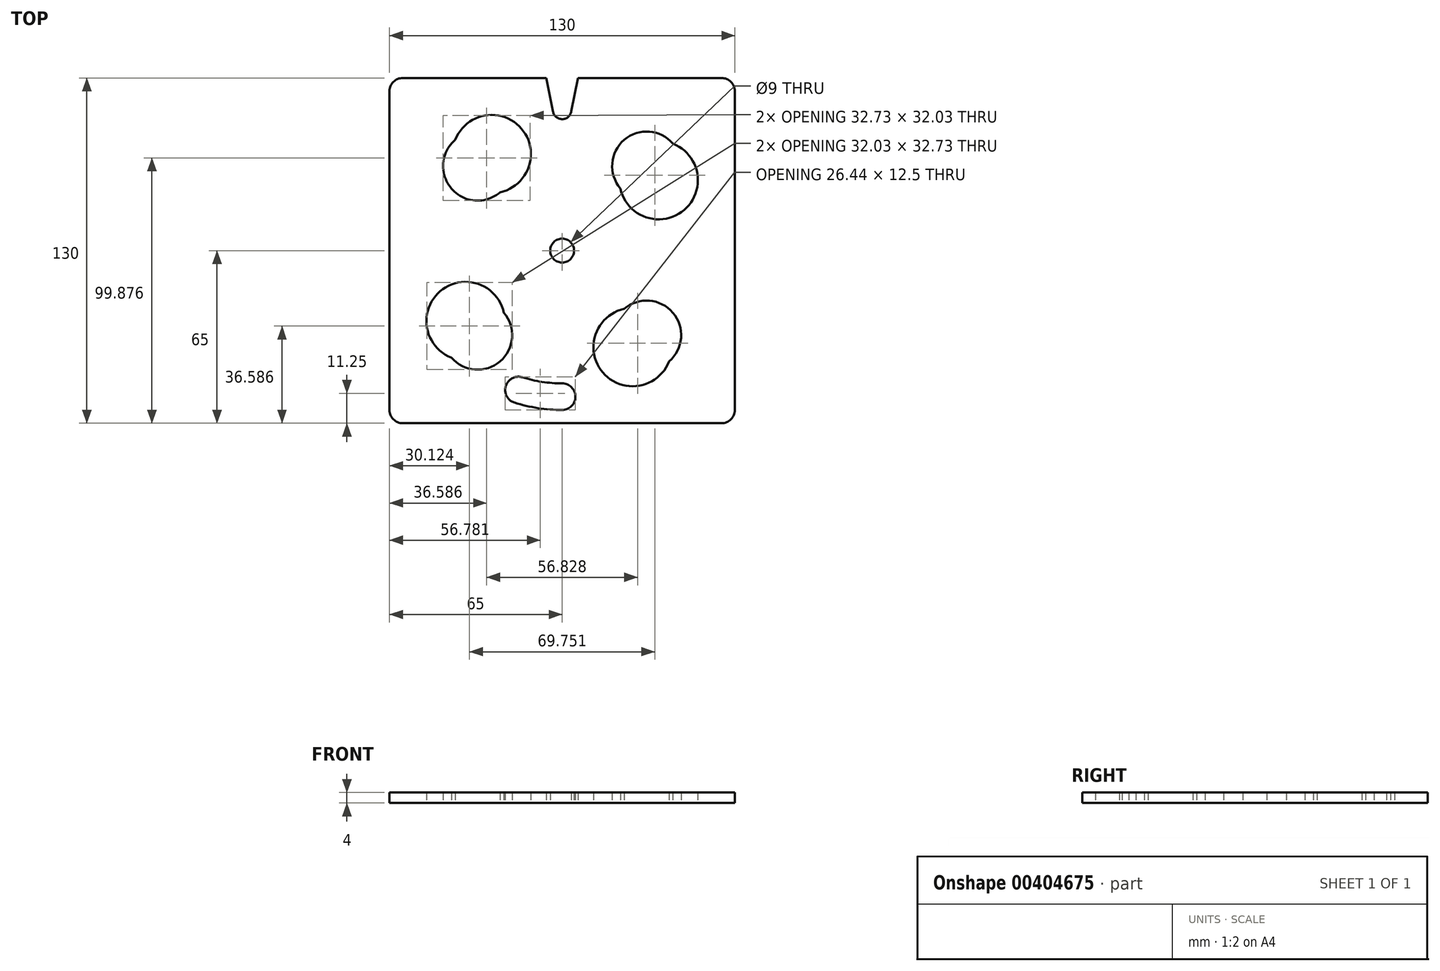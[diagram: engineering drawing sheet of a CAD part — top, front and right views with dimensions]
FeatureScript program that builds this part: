
annotation { "Feature Type Name" : "Feature", "Feature Type Description" : "" }
export const myFeature = defineFeature(function(context is Context, id is Id, definition is map)
    precondition{}
    {
        {
            var Q0;
            Q0=qCreatedBy(makeId("Top.planeOp"),FACE);
            var sketch = newSketch(context, id + "F0", { "sketchPlane" : qUnion([Q0])});
            skLineSegment(sketch, "E0.bottom", {"start": v(-60, 65) * mm, "end": v(-6, 65) * mm});
            skLineSegment(sketch, "E0.top", {"start": v(-60, -65) * mm, "end": v(60, -65) * mm});
            skLineSegment(sketch, "E0.right", {"start": v(65, 60) * mm, "end": v(65, -60) * mm});
            skArc(sketch, "E1", {"start": v(-40.27, 41.7) * mm, "mid": v(-41.7, 23.37) * mm, "end": v(-23.37, 21.94) * mm});
            skArc(sketch, "E2", {"start": v(-23.37, 21.94) * mm, "mid": v(-15.32, 45.94) * mm, "end": v(-40.27, 41.7) * mm});
            skArc(sketch, "E3.filletArc", {"start": v(-60, 65) * mm, "mid": v(-63.54, 63.54) * mm, "end": v(-65, 60) * mm});
            skPoint(sketch, "E4.visualSharp", {"position": v(65, 65) * mm});
            skArc(sketch, "E4.filletArc", {"start": v(65, 60) * mm, "mid": v(63.54, 63.54) * mm, "end": v(60, 65) * mm});
            skPoint(sketch, "E5.visualSharp", {"position": v(65, -65) * mm});
            skArc(sketch, "E5.filletArc", {"start": v(60, -65) * mm, "mid": v(63.54, -63.54) * mm, "end": v(65, -60) * mm});
            skLineSegment(sketch, "E6", {"start": v(-65, -60) * mm, "end": v(-65, 60) * mm});
            skLineSegment(sketch, "E7", {"start": v(-65, 0) * mm, "end": v(65, 0) * mm, "construction": true});
            skPoint(sketch, "E8.orphan", {"position": v(-65, -60) * mm});
            skPoint(sketch, "E9.visualSharp", {"position": v(-65, -65) * mm});
            skArc(sketch, "E9.filletArc", {"start": v(-65, -60) * mm, "mid": v(-63.54, -63.54) * mm, "end": v(-60, -65) * mm});
            skArc(sketch, "E10.1.0", {"start": v(-41.7, -40.27) * mm, "mid": v(-23.37, -41.7) * mm, "end": v(-21.94, -23.37) * mm});
            skArc(sketch, "E10.1.1", {"start": v(-21.94, -23.37) * mm, "mid": v(-45.94, -15.32) * mm, "end": v(-41.7, -40.27) * mm});
            skArc(sketch, "E10.2.0", {"start": v(40.27, -41.7) * mm, "mid": v(41.7, -23.37) * mm, "end": v(23.37, -21.94) * mm});
            skArc(sketch, "E10.2.1", {"start": v(23.37, -21.94) * mm, "mid": v(15.32, -45.94) * mm, "end": v(40.27, -41.7) * mm});
            skArc(sketch, "E10.3.0", {"start": v(41.7, 40.27) * mm, "mid": v(23.37, 41.7) * mm, "end": v(21.94, 23.37) * mm});
            skArc(sketch, "E10.3.1", {"start": v(21.94, 23.37) * mm, "mid": v(45.94, 15.32) * mm, "end": v(41.7, 40.27) * mm});
            skPoint(sketch, "E10.center", {"position": v(0, 0) * mm});
            skArc(sketch, "E11", {"start": v(0, -60) * mm, "mid": v(5, -55) * mm, "end": v(0, -50) * mm});
            skArc(sketch, "E12", {"start": v(-14.96, -47.7) * mm, "mid": v(-21.23, -50.98) * mm, "end": v(-17.95, -57.25) * mm});
            skArc(sketch, "E13", {"start": v(-14.96, -47.7) * mm, "mid": v(-7.57, -49.42) * mm, "end": v(0, -50) * mm});
            skArc(sketch, "E14", {"start": v(-17.95, -57.25) * mm, "mid": v(-9.08, -59.3) * mm, "end": v(0, -60) * mm});
            skLineSegment(sketch, "E15", {"start": v(-6, 65) * mm, "end": v(-3.43, 52.3) * mm});
            skLineSegment(sketch, "E16.MirrorCS", {"start": v(6, 65) * mm, "end": v(3.47, 52.54) * mm});
            skArc(sketch, "E17", {"start": v(-3.43, 52.3) * mm, "mid": v(0.12, 49.5) * mm, "end": v(3.47, 52.54) * mm});
            skLineSegment(sketch, "E18.trimOffspring", {"start": v(6, 65) * mm, "end": v(60, 65) * mm});
            skCircle(sketch, "E19", {"center": v(0, 0) * mm, "radius": 4.5 * mm});
            skLineSegment(sketch, "E20", {"start": v(0, 56.34) * mm, "end": v(0, -65) * mm, "construction": true});
            skLineSegment(sketch, "E21", {"start": v(-31.82, 31.82) * mm, "end": v(0, 0) * mm, "construction": true});
            skSolve(sketch);
        }
        {
            var Q0;
            Q0=makeQuery(id+"F0.imprint","IMPRINT",FACE,{"disambiguationData":[TD([[makeQuery(id+"F0.imprint","IMPRINT",EDGE,{"derivedFrom":sQuery(id+"F0.wireOp",EDGE,"E0.bottom")}),-1.0]])]});
            extrude(context, id + "F1", {"entities" : qUnion([Q0]), "depth" : 4 * mm});
        }
    });
